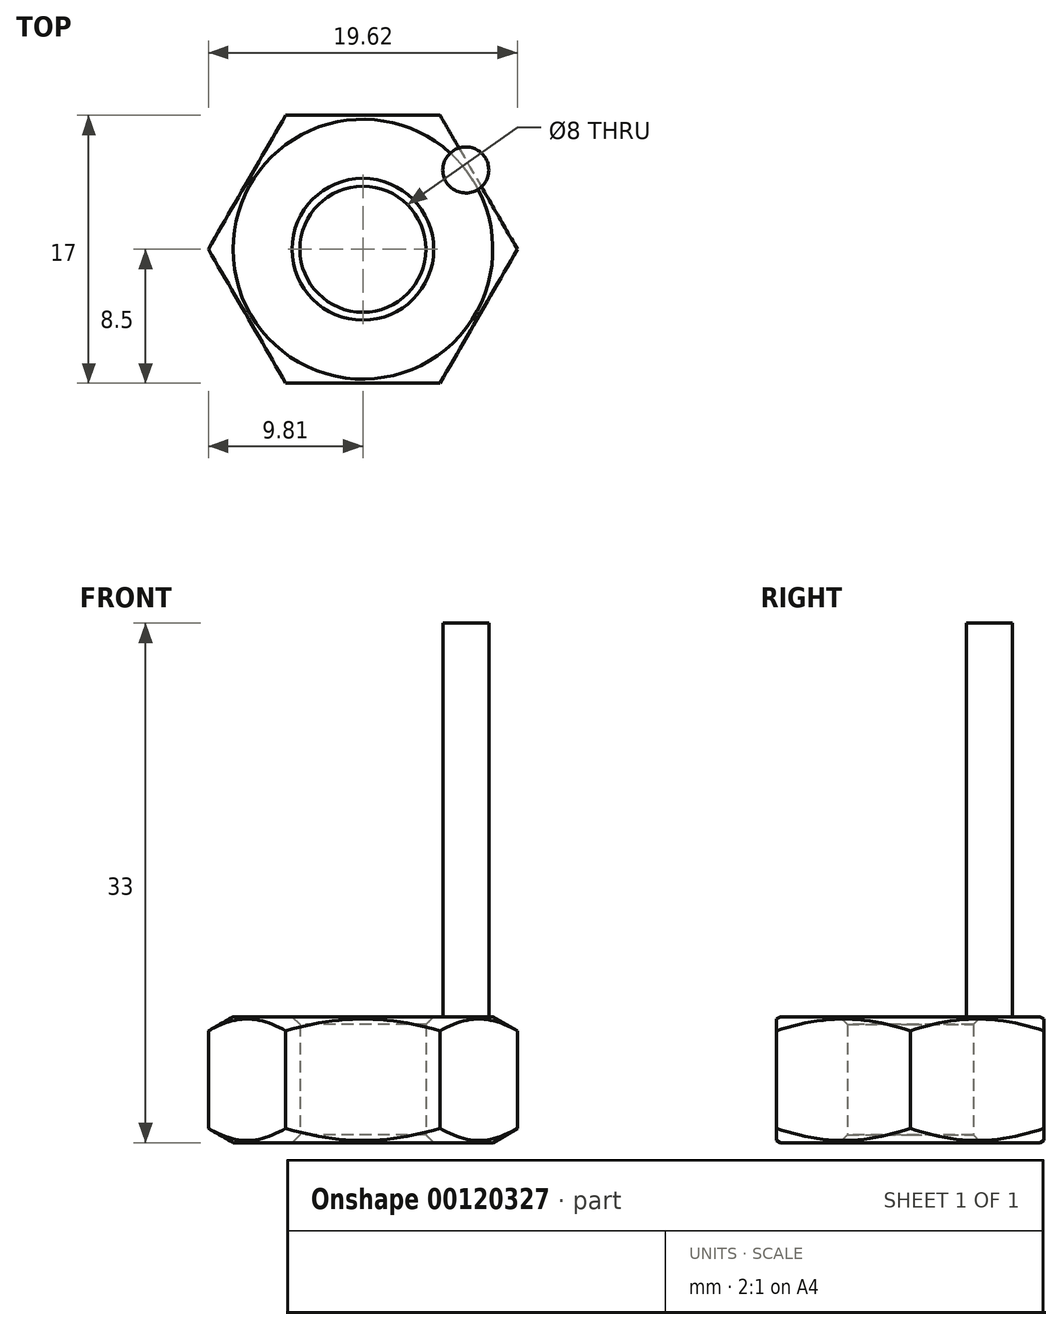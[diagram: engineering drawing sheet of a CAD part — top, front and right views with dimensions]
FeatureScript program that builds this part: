
annotation { "Feature Type Name" : "Feature", "Feature Type Description" : "" }
export const myFeature = defineFeature(function(context is Context, id is Id, definition is map)
    precondition{}
    {
        {
            var Q0;
            Q0=qCreatedBy(makeId("Top.planeOp"),FACE);
            var sketch = newSketch(context, id + "F0", { "sketchPlane" : qUnion([Q0])});
            skCircle(sketch, "E0.cCircle", {"center": v(0, 0) * mm, "radius": 8.5 * mm, "construction": true});
            skLineSegment(sketch, "E0.0", {"start": v(9.81, 0) * mm, "end": v(4.9, -8.5) * mm});
            skLineSegment(sketch, "E0.1", {"start": v(4.9, -8.5) * mm, "end": v(-4.9, -8.5) * mm});
            skLineSegment(sketch, "E0.2", {"start": v(-4.9, -8.5) * mm, "end": v(-9.81, 0) * mm});
            skLineSegment(sketch, "E0.3", {"start": v(-9.81, 0) * mm, "end": v(-4.9, 8.5) * mm});
            skLineSegment(sketch, "E0.4", {"start": v(-4.9, 8.5) * mm, "end": v(4.9, 8.5) * mm});
            skLineSegment(sketch, "E0.5", {"start": v(4.9, 8.5) * mm, "end": v(9.81, 0) * mm});
            skPoint(sketch, "E0.0.midPoint", {"position": v(7.36, -4.25) * mm});
            skCircle(sketch, "E1", {"center": v(0, 0) * mm, "radius": 4 * mm});
            skSolve(sketch);
        }
        {
            var Q0;
            Q0 = qSketchRegion(id + "F0", true);
            var Q1;
            Q1=makeQuery(id+"F0.imprint","IMPRINT",FACE,{"disambiguationData":[TD([[makeQuery(id+"F0.imprint","IMPRINT",EDGE,{"derivedFrom":sQuery(id+"F0.wireOp",EDGE,"E0.0")}),-1.0]])]});
            extrude(context, id + "F1", {"entities" : qUnion([Q0, Q1]), "depth" : 8 * mm});
        }
        {
            var Q0;
            Q0=qCreatedBy(makeId("Front.planeOp"),FACE);
            var sketch = newSketch(context, id + "F2", { "sketchPlane" : qUnion([Q0])});
            skLineSegment(sketch, "E2", {"start": v(0, 15.63) * mm, "end": v(0, -8.74) * mm, "construction": true});
            skLineSegment(sketch, "E3", {"start": v(8.25, 8) * mm, "end": v(12.5, 8) * mm});
            skLineSegment(sketch, "E4", {"start": v(12.5, 8) * mm, "end": v(12.5, 5.55) * mm});
            skLineSegment(sketch, "E5", {"start": v(12.5, 5.55) * mm, "end": v(8.25, 8) * mm});
            skLineSegment(sketch, "E6", {"start": v(-9.67, 4) * mm, "end": v(12.2, 4) * mm, "construction": true});
            skLineSegment(sketch, "E7.MirrorCS", {"start": v(8.25, 0) * mm, "end": v(12.5, 0) * mm});
            skLineSegment(sketch, "E8.MirrorCS", {"start": v(12.5, 2.45) * mm, "end": v(8.25, 0) * mm});
            skLineSegment(sketch, "E9.MirrorCS", {"start": v(12.5, 0) * mm, "end": v(12.5, 2.45) * mm});
            skSolve(sketch);
        }
        {
            var Q0;
            Q0 = qSketchRegion(id + "F2", true);
            var Q1;
            Q1=sQuery(id+"F2.wireOp",EDGE,"E2");
            revolve(context, id + "F3", {"operationType" : NewBodyOperationType.REMOVE, "entities" : qUnion([Q0]), "axis" : qUnion([Q1]), "revolveType" : RevolveType.FULL, "oppositeDirection" : true});
        }
        {
            var Q0;
            Q0=makeQuery(id+"F1.opExtrude","CAP_EDGE",EDGE,{"disambiguationData":[OSD([sQuery(id+"F0.wireOp",EDGE,"E1")])],"isStart":false});
            var Q1;
            Q1=makeQuery(id+"F1.opExtrude","CAP_EDGE",EDGE,{"disambiguationData":[OSD([sQuery(id+"F0.wireOp",EDGE,"E1")])],"isStart":true});
            chamfer(context, id + "F4", {"entities" : qUnion([Q0, Q1]), "width" : 0.5 * mm, "tangentPropagation" : true});
        }
        {
            var Q0;
            Q0=makeQuery(id+"F1.opExtrude","CAP_FACE",FACE,{"disambiguationData":[OSD([sQuery(id+"F0.wireOp",EDGE,"E0.0"),sQuery(id+"F0.wireOp",EDGE,"E0.1"),sQuery(id+"F0.wireOp",EDGE,"E0.2"),sQuery(id+"F0.wireOp",EDGE,"E0.3"),sQuery(id+"F0.wireOp",EDGE,"E0.4"),sQuery(id+"F0.wireOp",EDGE,"E0.5"),sQuery(id+"F0.wireOp",EDGE,"E1")])],"isStart":false});
            var sketch = newSketch(context, id + "F5", { "sketchPlane" : qUnion([Q0])});
            skCircle(sketch, "E10", {"center": v(6.54, 5.03) * mm, "radius": 1.46 * mm});
            skSolve(sketch);
        }
        {
            var Q0;
            Q0 = qSketchRegion(id + "F5", true);
            extrude(context, id + "F6", {"entities" : qUnion([Q0]), "operationType" : NewBodyOperationType.ADD, "depth" : 25 * mm, "offsetDistance" : 25 * mm});
        }
    });
